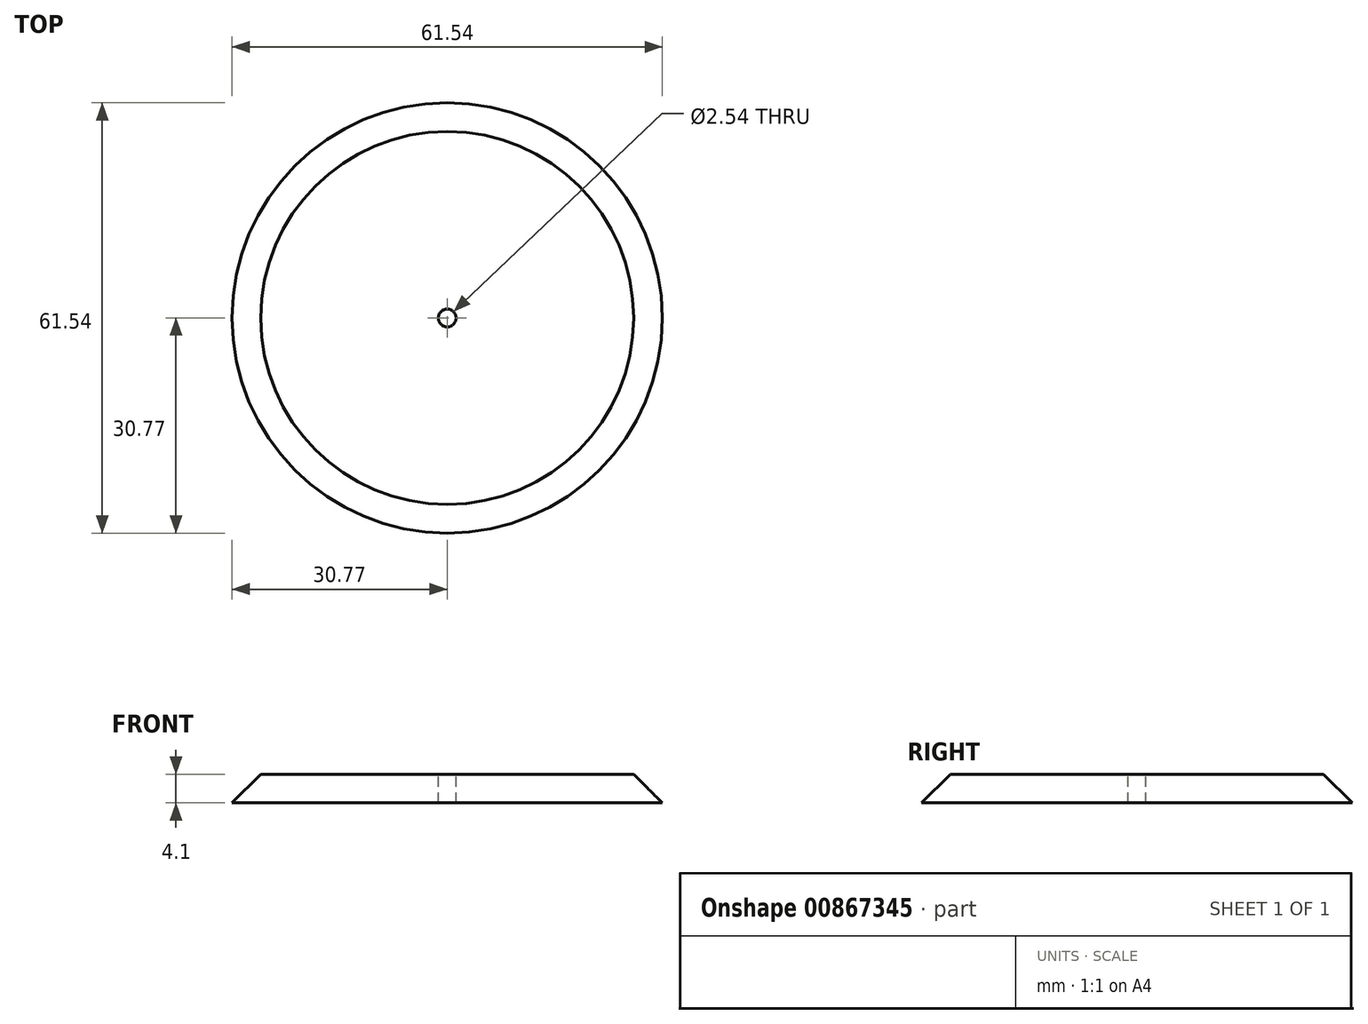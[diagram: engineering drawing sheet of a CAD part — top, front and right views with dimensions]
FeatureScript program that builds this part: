
annotation { "Feature Type Name" : "Feature", "Feature Type Description" : "" }
export const myFeature = defineFeature(function(context is Context, id is Id, definition is map)
    precondition{}
    {
        {
            var Q0;
            Q0=qCreatedBy(makeId("Top.planeOp"),FACE);
            var sketch = newSketch(context, id + "F0", { "sketchPlane" : qUnion([Q0])});
            skCircle(sketch, "E0", {"center": v(0, 0) * mm, "radius": 31.75 * mm});
            skSolve(sketch);
        }
        {
            var Q0;
            Q0=makeQuery(id+"F0.imprint","IMPRINT",FACE,{"disambiguationData":[TD([[makeQuery(id+"F0.imprint","IMPRINT",EDGE,{"derivedFrom":sQuery(id+"F0.wireOp",EDGE,"E0")}),1.0]])]});
            extrude(context, id + "F1", {"entities" : qUnion([Q0]), "depth" : 4.1 * mm, "offsetDistance" : 25.4 * mm});
        }
        {
            var Q0;
            Q0=makeQuery(id+"F1.opExtrude","CAP_EDGE",EDGE,{"disambiguationData":[OSD([sQuery(id+"F0.wireOp",EDGE,"E0")])],"isStart":false});
            chamfer(context, id + "F2", {"entities" : qUnion([Q0]), "width" : 5.08 * mm, "tangentPropagation" : true});
        }
        {
            var Q0;
            Q0=makeQuery(id+"F1.opExtrude","CAP_FACE",FACE,{"disambiguationData":[OSD([sQuery(id+"F0.wireOp",EDGE,"E0")])],"isStart":false});
            var sketch = newSketch(context, id + "F3", { "sketchPlane" : qUnion([Q0])});
            skSolve(sketch);
        }
        {
            var Q0;
            {var subQ0=sQuery(id+"F0.wireOp",EDGE,"E0");Q0=makeQuery(id+"F3.imprint","IMPRINT",FACE,{"disambiguationData":[TD([[makeQuery(id+"F3.imprint","IMPRINT",EDGE,{"derivedFrom":makeQuery(id+"F2.opChamfer","BLEND_EDGE",EDGE,{"blendedFrom":[makeQuery(id+"F1.opExtrude","CAP_EDGE",EDGE,{"disambiguationData":[OSD([subQ0])],"isStart":false}),makeQuery(id+"F1.opExtrude","CAP_FACE",FACE,{"disambiguationData":[OSD([subQ0])],"isStart":false})],"blendedInto":[makeQuery(id+"F1.opExtrude","CAP_FACE",FACE,{"disambiguationData":[OSD([subQ0])],"isStart":false})]})}),1.0]])]});}
            var sketch = newSketch(context, id + "F4", { "sketchPlane" : qUnion([Q0])});
            skPoint(sketch, "E1", {"position": v(0, 0) * mm});
            skSolve(sketch);
        }
        {
            var Q0;
            Q0=sQuery(id+"F4.wireOp",VERTEX,"E1");
            var Q1;
            Q1=makeQuery(id+"F1.opExtrude","SWEPT_BODY",BODY,{"disambiguationData":[OSD([sQuery(id+"F0.wireOp",EDGE,"E0")])]});
            hole(context, id + "F5", {"style" : HoleStyle.SIMPLE, "endStyle" : HoleEndStyle.THROUGH, "holeDiameter" : 2.54 * mm, "majorDiameter" : 6.35 * mm, "isTappedThrough" : true, "tappedDepth" : 12.7 * mm, "tapClearance" : 3, "locations" : qUnion([Q0]), "scope" : qUnion([Q1])});
        }
        {
            var Q0;
            {var subQ0=sQuery(id+"F0.wireOp",EDGE,"E0");Q0=makeQuery(id+"F3.imprint","IMPRINT",FACE,{"disambiguationData":[TD([[makeQuery(id+"F3.imprint","IMPRINT",EDGE,{"derivedFrom":makeQuery(id+"F2.opChamfer","BLEND_EDGE",EDGE,{"blendedFrom":[makeQuery(id+"F1.opExtrude","CAP_EDGE",EDGE,{"disambiguationData":[OSD([subQ0])],"isStart":false}),makeQuery(id+"F1.opExtrude","CAP_FACE",FACE,{"disambiguationData":[OSD([subQ0])],"isStart":false})],"blendedInto":[makeQuery(id+"F1.opExtrude","CAP_FACE",FACE,{"disambiguationData":[OSD([subQ0])],"isStart":false})]})}),1.0]])]});}
            var sketch = newSketch(context, id + "F6", { "sketchPlane" : qUnion([Q0])});
            skLineSegment(sketch, "E2.bottom", {"start": v(8.24, -5.56) * mm, "end": v(-8.27, -5.56) * mm});
            skLineSegment(sketch, "E2.top", {"start": v(8.24, 7.14) * mm, "end": v(-8.27, 7.14) * mm});
            skLineSegment(sketch, "E2.left", {"start": v(8.24, -5.56) * mm, "end": v(8.24, 7.14) * mm});
            skLineSegment(sketch, "E2.right", {"start": v(-8.27, -5.56) * mm, "end": v(-8.27, 7.14) * mm});
            skPoint(sketch, "E2.middle", {"position": v(-0.02, 0.8) * mm});
            skSolve(sketch);
        }
        {
            var Q0;
            Q0 = qSketchRegion(id + "F6", true);
            var Q1;
            Q1=sQuery(id+"F6.wireOp",EDGE,"E2.bottom");
            var Q2;
            Q2=sQuery(id+"F6.wireOp",EDGE,"E2.right");
            var Q3;
            Q3=sQuery(id+"F6.wireOp",EDGE,"E2.left");
            var Q4;
            Q4=sQuery(id+"F6.wireOp",EDGE,"E2.top");
            extrude(context, id + "F7", {"entities" : qUnion([Q0]), "bodyType" : ToolBodyType.SURFACE, "surfaceEntities" : qUnion([Q1, Q2, Q3, Q4]), "depth" : 21.59 * mm, "offsetDistance" : 25.4 * mm});
        }
    });
